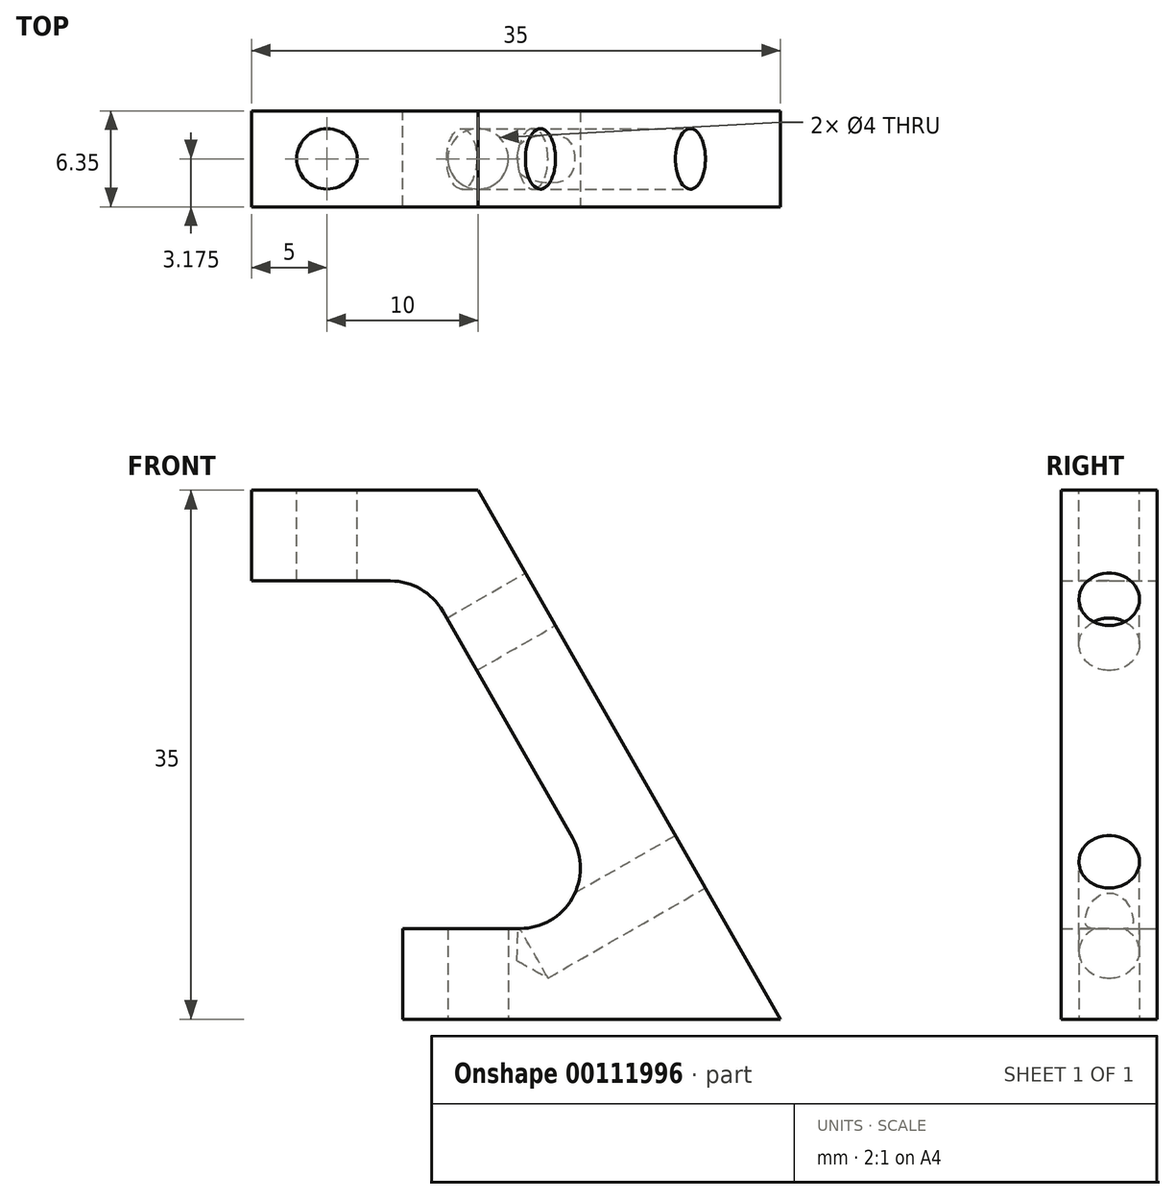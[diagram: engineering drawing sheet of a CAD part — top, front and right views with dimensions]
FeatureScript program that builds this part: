
annotation { "Feature Type Name" : "Feature", "Feature Type Description" : "" }
export const myFeature = defineFeature(function(context is Context, id is Id, definition is map)
    precondition{}
    {
        {
            var Q0;
            Q0=qCreatedBy(makeId("Front.planeOp"),FACE);
            var sketch = newSketch(context, id + "F0", { "sketchPlane" : qUnion([Q0])});
            skLineSegment(sketch, "E0", {"start": v(0, 0) * mm, "end": v(15, 0) * mm});
            skLineSegment(sketch, "E1", {"start": v(15, 0) * mm, "end": v(35, -35) * mm});
            skLineSegment(sketch, "E2", {"start": v(35, -35) * mm, "end": v(10, -35) * mm});
            skLineSegment(sketch, "E3", {"start": v(10, -35) * mm, "end": v(10, -29) * mm});
            skLineSegment(sketch, "E4", {"start": v(10, -29) * mm, "end": v(24.66, -29) * mm});
            skLineSegment(sketch, "E5", {"start": v(24.66, -29) * mm, "end": v(11.52, -6) * mm});
            skLineSegment(sketch, "E6", {"start": v(11.52, -6) * mm, "end": v(0, -6) * mm});
            skLineSegment(sketch, "E7", {"start": v(0, -6) * mm, "end": v(0, 0) * mm});
            skSolve(sketch);
        }
        {
            var Q0;
            Q0 = qSketchRegion(id + "F0", true);
            extrude(context, id + "F1", {"entities" : qUnion([Q0]), "depth" : 6.35 * mm});
        }
        {
            var Q0;
            Q0=makeQuery(id+"F1.opExtrude","SWEPT_FACE",FACE,{"disambiguationData":[OSD([sQuery(id+"F0.wireOp",EDGE,"E0")])]});
            var sketch = newSketch(context, id + "F2", { "sketchPlane" : qUnion([Q0])});
            skCircle(sketch, "E8", {"center": v(5, -3.18) * mm, "radius": 2 * mm});
            skPoint(sketch, "E9", {"position": v(15, -3.17) * mm});
            skSolve(sketch);
        }
        {
            var Q0;
            Q0 = qSketchRegion(id + "F2", true);
            extrude(context, id + "F3", {"entities" : qUnion([Q0]), "operationType" : NewBodyOperationType.REMOVE, "endBound" : BoundingType.UP_TO_NEXT, "oppositeDirection" : true, "depth" : 25 * mm});
        }
        {
            var Q0;
            Q0=makeQuery(id+"F1.opExtrude","SWEPT_FACE",FACE,{"disambiguationData":[OSD([sQuery(id+"F0.wireOp",EDGE,"E2")])]});
            var sketch = newSketch(context, id + "F4", { "sketchPlane" : qUnion([Q0])});
            skCircle(sketch, "E10", {"center": v(15, 3.17) * mm, "radius": 2 * mm});
            skPoint(sketch, "E11", {"position": v(35, 3.17) * mm});
            skSolve(sketch);
        }
        {
            var Q0;
            Q0 = qSketchRegion(id + "F4", true);
            extrude(context, id + "F5", {"entities" : qUnion([Q0]), "operationType" : NewBodyOperationType.REMOVE, "oppositeDirection" : true, "depth" : 12 * mm});
        }
        {
            var Q0;
            Q0=makeQuery(id+"F1.opExtrude","SWEPT_EDGE",EDGE,{"disambiguationData":[OSD([sQuery(id+"F0.wireOp",EDGE,"E5"),sQuery(id+"F0.wireOp",EDGE,"E6")])]});
            var Q1;
            Q1=makeQuery(id+"F1.opExtrude","SWEPT_EDGE",EDGE,{"disambiguationData":[OSD([sQuery(id+"F0.wireOp",EDGE,"E4"),sQuery(id+"F0.wireOp",EDGE,"E5")])]});
            fillet(context, id + "F6", {"entities" : qUnion([Q0, Q1]), "radius" : 4 * mm, "tangentPropagation" : true, "allowEdgeOverflow" : false});
        }
        {
            var Q0;
            Q0=makeQuery(id+"F1.opExtrude","SWEPT_FACE",FACE,{"disambiguationData":[OSD([sQuery(id+"F0.wireOp",EDGE,"E1")])]});
            var sketch = newSketch(context, id + "F7", { "sketchPlane" : qUnion([Q0])});
            skPoint(sketch, "E12", {"position": v(-3.17, -47.75) * mm});
            skPoint(sketch, "E13", {"position": v(-3.18, -35.75) * mm});
            skPoint(sketch, "E14", {"position": v(-3.18, -15.75) * mm});
            skSolve(sketch);
        }
        {
            var Q0;
            Q0=sQuery(id+"F7.wireOp",VERTEX,"E14");
            var Q1;
            Q1=sQuery(id+"F7.wireOp",VERTEX,"E13");
            var Q2;
            Q2=makeQuery(id+"F1.opExtrude","SWEPT_BODY",BODY,{"disambiguationData":[OSD([sQuery(id+"F0.wireOp",EDGE,"E0"),sQuery(id+"F0.wireOp",EDGE,"E1"),sQuery(id+"F0.wireOp",EDGE,"E2"),sQuery(id+"F0.wireOp",EDGE,"E3"),sQuery(id+"F0.wireOp",EDGE,"E4"),sQuery(id+"F0.wireOp",EDGE,"E5"),sQuery(id+"F0.wireOp",EDGE,"E6"),sQuery(id+"F0.wireOp",EDGE,"E7")])]});
            hole(context, id + "F8", {"style" : HoleStyle.SIMPLE, "endStyle" : HoleEndStyle.BLIND, "holeDiameter" : 4 * mm, "holeDepth" : 12 * mm, "locations" : qUnion([Q0, Q1]), "scope" : qUnion([Q2])});
        }
    });
